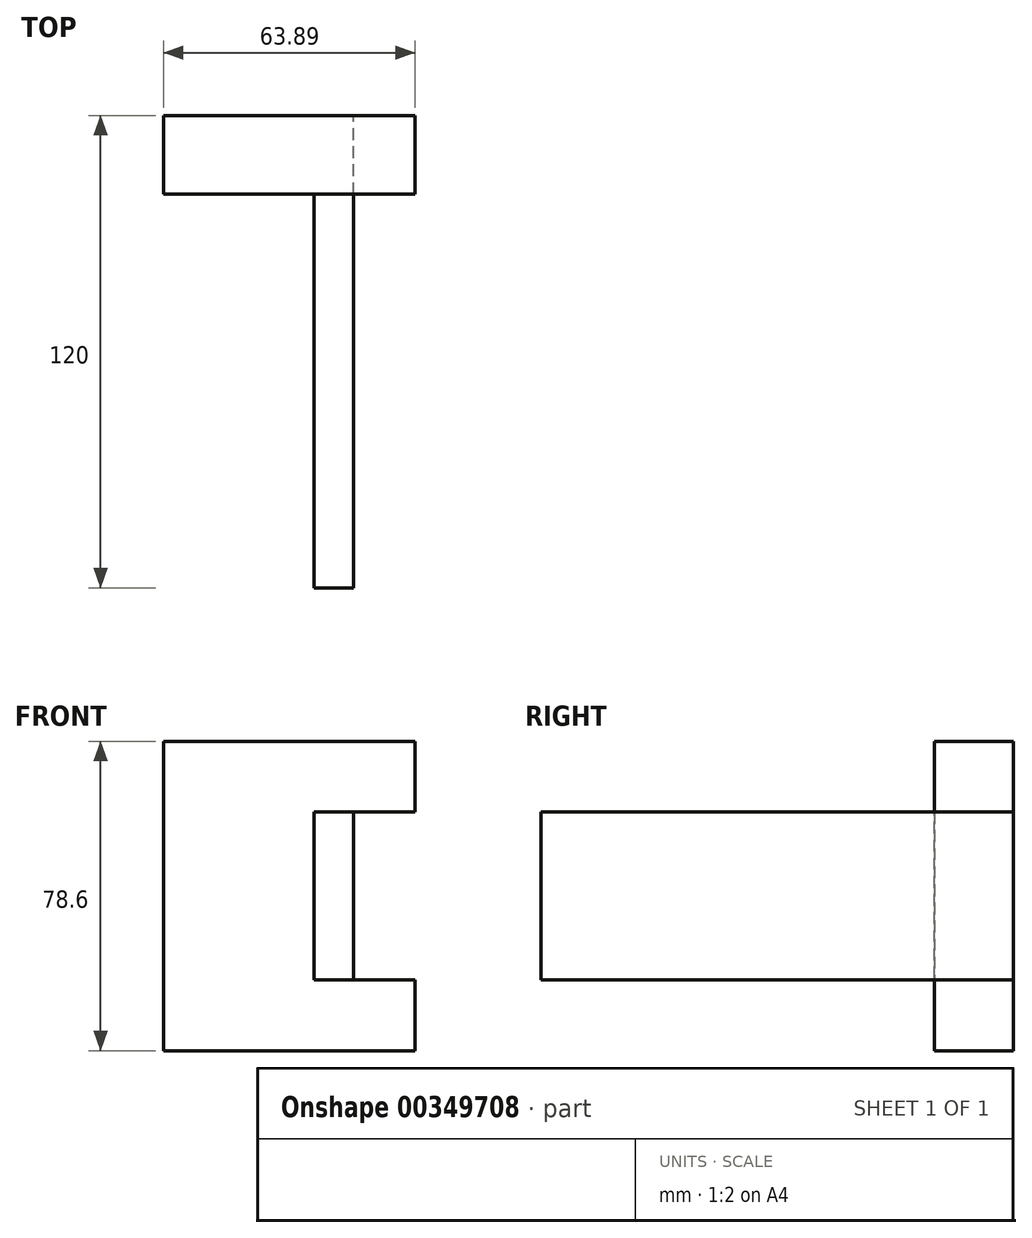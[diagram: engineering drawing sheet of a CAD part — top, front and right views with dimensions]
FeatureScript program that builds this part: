
annotation { "Feature Type Name" : "Feature", "Feature Type Description" : "" }
export const myFeature = defineFeature(function(context is Context, id is Id, definition is map)
    precondition{}
    {
        {
            var Q0;
            Q0=qCreatedBy(makeId("Front.planeOp"),FACE);
            var sketch = newSketch(context, id + "F0", { "sketchPlane" : qUnion([Q0])});
            skLineSegment(sketch, "E0", {"start": v(-29.59, 0) * mm, "end": v(-29.59, 39.3) * mm});
            skLineSegment(sketch, "E1", {"start": v(-29.59, 39.3) * mm, "end": v(34.3, 39.3) * mm});
            skLineSegment(sketch, "E2", {"start": v(34.3, 39.3) * mm, "end": v(34.3, 21.34) * mm});
            skLineSegment(sketch, "E3", {"start": v(34.3, 21.34) * mm, "end": v(18.7, 21.34) * mm});
            skLineSegment(sketch, "E4", {"start": v(18.7, 21.34) * mm, "end": v(18.7, 0) * mm});
            skLineSegment(sketch, "E5.MirrorCS", {"start": v(-29.59, 0) * mm, "end": v(-29.59, -39.3) * mm});
            skLineSegment(sketch, "E6.MirrorCS", {"start": v(-29.59, -39.3) * mm, "end": v(34.3, -39.3) * mm});
            skLineSegment(sketch, "E7.MirrorCS", {"start": v(34.3, -39.3) * mm, "end": v(34.3, -21.34) * mm});
            skLineSegment(sketch, "E8.MirrorCS", {"start": v(34.3, -21.34) * mm, "end": v(18.7, -21.34) * mm});
            skLineSegment(sketch, "E9.MirrorCS", {"start": v(18.7, -21.34) * mm, "end": v(18.7, 0) * mm});
            skSolve(sketch);
        }
        {
            var Q0;
            Q0 = qSketchRegion(id + "F0", true);
            extrude(context, id + "F1", {"entities" : qUnion([Q0]), "depth" : 20 * mm});
        }
        {
            var Q0;
            Q0=makeQuery(id+"F1.opExtrude","CAP_FACE",FACE,{"disambiguationData":[OSD([sQuery(id+"F0.wireOp",EDGE,"E0"),sQuery(id+"F0.wireOp",EDGE,"E1"),sQuery(id+"F0.wireOp",EDGE,"E2"),sQuery(id+"F0.wireOp",EDGE,"E3"),sQuery(id+"F0.wireOp",EDGE,"E4"),sQuery(id+"F0.wireOp",EDGE,"E5.MirrorCS"),sQuery(id+"F0.wireOp",EDGE,"E6.MirrorCS"),sQuery(id+"F0.wireOp",EDGE,"E7.MirrorCS"),sQuery(id+"F0.wireOp",EDGE,"E8.MirrorCS"),sQuery(id+"F0.wireOp",EDGE,"E9.MirrorCS")])],"isStart":false});
            var sketch = newSketch(context, id + "F2", { "sketchPlane" : qUnion([Q0])});
            skLineSegment(sketch, "E10.bottom", {"start": v(18.7, 21.34) * mm, "end": v(8.68, 21.34) * mm});
            skLineSegment(sketch, "E10.top", {"start": v(18.7, -21.34) * mm, "end": v(8.68, -21.34) * mm});
            skLineSegment(sketch, "E10.left", {"start": v(18.7, 21.34) * mm, "end": v(18.7, -21.34) * mm});
            skLineSegment(sketch, "E10.right", {"start": v(8.68, 21.34) * mm, "end": v(8.68, -21.34) * mm});
            skSolve(sketch);
        }
        {
            var Q0;
            Q0 = qSketchRegion(id + "F2", true);
            extrude(context, id + "F3", {"entities" : qUnion([Q0]), "operationType" : NewBodyOperationType.ADD, "depth" : 100 * mm});
        }
    });
